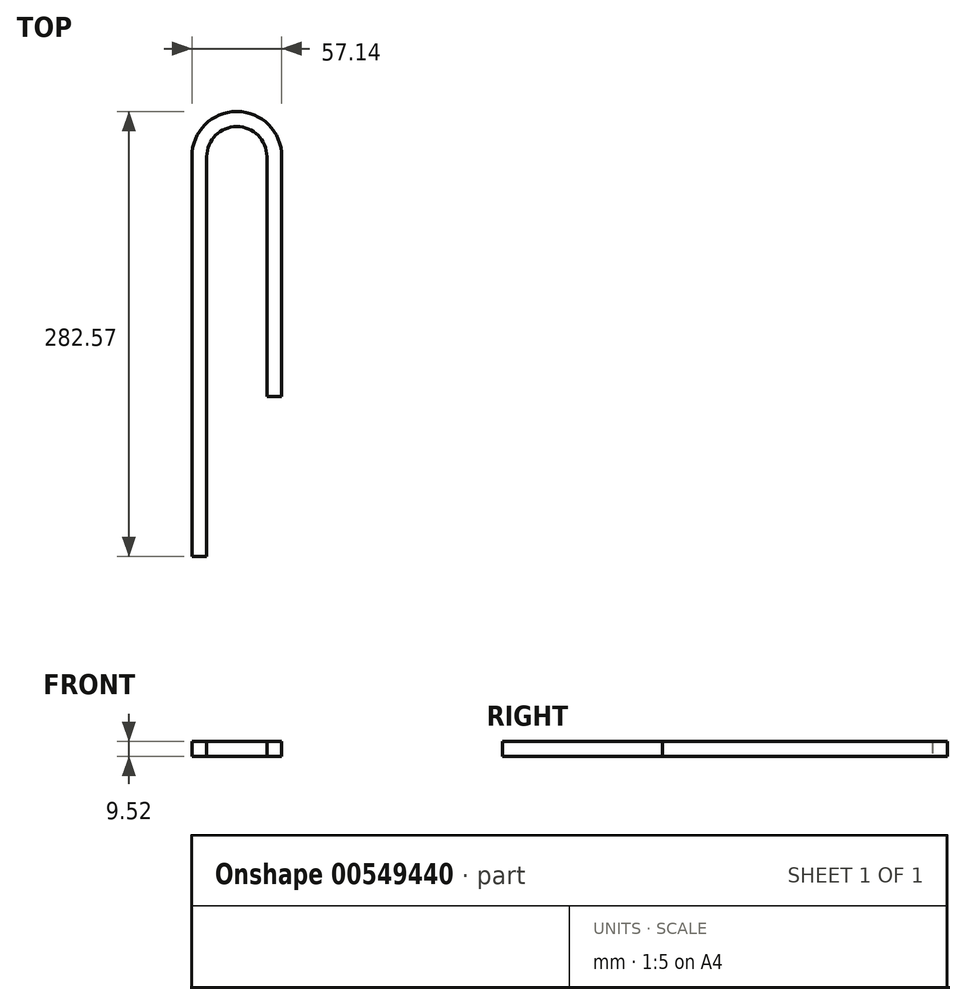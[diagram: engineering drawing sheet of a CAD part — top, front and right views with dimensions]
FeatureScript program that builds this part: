
annotation { "Feature Type Name" : "Feature", "Feature Type Description" : "" }
export const myFeature = defineFeature(function(context is Context, id is Id, definition is map)
    precondition{}
    {
        {
            var Q0;
            Q0=qCreatedBy(makeId("Top.planeOp"),FACE);
            var sketch = newSketch(context, id + "F0", { "sketchPlane" : qUnion([Q0])});
            skArc(sketch, "E0", {"start": v(23.81, 0) * mm, "mid": v(0, 23.81) * mm, "end": v(-23.81, 0) * mm});
            skLineSegment(sketch, "E1", {"start": v(-23.81, 0) * mm, "end": v(-23.81, -254) * mm});
            skLineSegment(sketch, "E2", {"start": v(23.81, 0) * mm, "end": v(23.81, -152.4) * mm});
            skSolve(sketch);
        }
        {
            var Q0;
            Q0=qCreatedBy(makeId("Front.planeOp"),FACE);
            cPlane(context, id + "F1", {"entities" : qUnion([Q0]), "cplaneType" : CPlaneType.OFFSET, "offset" : 254 * mm, "width" : 152.4 * mm, "height" : 152.4 * mm});
        }
        {
            var Q0;
            Q0=qCreatedBy(id+"F1.planeOp",FACE);
            var sketch = newSketch(context, id + "F2", { "sketchPlane" : qUnion([Q0])});
            skLineSegment(sketch, "E3.0", {"start": v(-23.81, 0) * mm, "end": v(23.81, 0) * mm});
            skLineSegment(sketch, "E4.bottom", {"start": v(-28.58, 4.76) * mm, "end": v(-19.05, 4.76) * mm});
            skLineSegment(sketch, "E4.top", {"start": v(-28.58, -4.76) * mm, "end": v(-19.05, -4.76) * mm});
            skLineSegment(sketch, "E4.left", {"start": v(-28.58, 4.76) * mm, "end": v(-28.58, -4.76) * mm});
            skLineSegment(sketch, "E4.right", {"start": v(-19.05, 4.76) * mm, "end": v(-19.05, -4.76) * mm});
            skPoint(sketch, "E4.middle", {"position": v(-23.81, 0) * mm});
            skSolve(sketch);
        }
        {
            var Q0;
            {var subQ0=sQuery(id+"F2.wireOp",EDGE,"E4.bottom");Q0=makeQuery(id+"F2.imprint","IMPRINT",FACE,{"disambiguationData":[TD([[makeQuery(id+"F2.imprint","IMPRINT",EDGE,{"derivedFrom":subQ0}),-1.0]])]});}
            var Q1;
            Q1=sQuery(id+"F0.wireOp",EDGE,"E1");
            var Q2;
            Q2=sQuery(id+"F0.wireOp",EDGE,"E0");
            var Q3;
            Q3=sQuery(id+"F0.wireOp",EDGE,"E2");
            sweep(context, id + "F3", {"profiles" : qUnion([Q0]), "path" : qUnion([Q1, Q2, Q3])});
        }
    });
